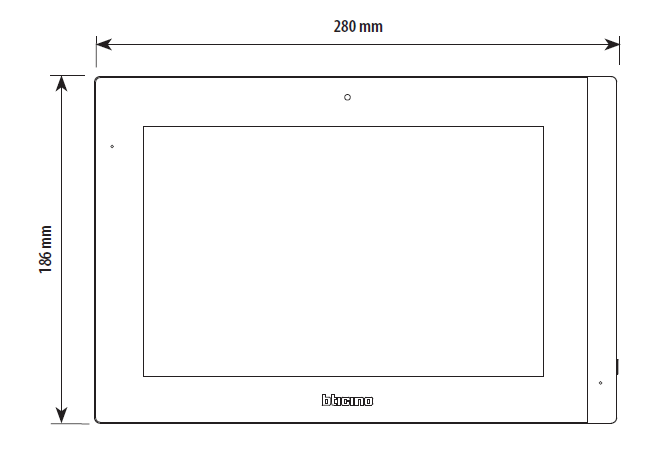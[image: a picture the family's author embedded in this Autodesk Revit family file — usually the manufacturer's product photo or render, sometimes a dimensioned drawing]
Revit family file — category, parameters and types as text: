
# Revit family: Legrand-Hotel_UX_ONE-Thermostat-With Service
name_source: partatom
category: Equipement électrique
units: mm (PartAtom-declared; Revit-internal decimal feet)

## family parameters
Configuration du panneau = Deux colonnes, circuits au sein
Cote de connecteur circulaire = Utiliser le diamètre
Couper avec des vides une fois chargée = Non
Hôte = Face
Partagée = Non
Point de calcul de pièce = Non
Type d'élément = Tableau de raccordement

## types (8) — shared parameters
Built-in depth = 50 mm  [stored 0.164042 ft]
Configurator website = https://uxforhotels.legrand.com
Do not disturb function = Oui
Elévation par défaut = 1500 mm  [stored 4.92126 ft]
Fabricant = LEGRAND
General Conditions of Use = https://export.legrand.com
Height = 93 mm  [stored 0.305118 ft]
IK = 04
IP = 20
Manual setpoint adjustment = Oui
Material = Plastic
Parallel operation possible = Oui
Radio bus system = Oui
Touchscreen = Oui
Width = 129 mm  [stored 0.423228 ft]
With display = Oui

## per-type parameters (varying)
| type | Color | Depth | Hauteur pictogrammes | Hauteur vide | Installation method | Matériau plaque | Matériau écran | Plaque apparente | Plaque encastrée | Product designation | Reference | Tension |
| Black 230V Recessed DND MUR | Black | 52 mm | 0 mm  [stored 0 ft] | -40 mm  [stored -0.131234 ft] | Flush-mounting | LEGRAND_BLACK_PLASTIC | LEGRAND_BLACK_SCREEN | Non | Oui | FLUSH MOUNTING HOTEL THERMOSTAT BLACK 230V WITH DND MUR | LG-048915 | 230 V AC |
| Black 230V Surface DND MUR | Black | 28 mm  [stored 0.0918635 ft] | 16 mm | 0 mm  [stored 0 ft] | surface | LEGRAND_BLACK_PLASTIC | LEGRAND_BLACK_SCREEN | Oui | Non | SURFACE HOTEL THERMOSTAT BLACK  230V WITH DND MUR | LG-048923 | 230 V AC |
| White 230V Recessed DND MUR | White | 52 mm | 0 mm  [stored 0 ft] | -40 mm  [stored -0.131234 ft] | Flush-mounting | LEGRAND_WHITE_PLASTIC | LEGRAND_WHITE_SCREEN | Non | Oui | FLUSH MOUNTING HOTEL THERMOSTAT WHITE 230V WITH DND MUR | LG-048924 | 230 V AC |
| White 230V Surface DND MUR | White | 28 mm  [stored 0.0918635 ft] | 16 mm | 0 mm  [stored 0 ft] | surface | LEGRAND_WHITE_PLASTIC | LEGRAND_WHITE_SCREEN | Oui | Non | SURFACE HOTEL THERMOSTAT WHITE 230V WITH DND MUR | LG-048925 | 230 V AC |
| Black 24V Recessed DND MUR | Black | 52 mm | 0 mm  [stored 0 ft] | -40 mm  [stored -0.131234 ft] | Flush-mounting | LEGRAND_BLACK_PLASTIC | LEGRAND_BLACK_SCREEN | Non | Oui | FLUSH MOUNTING HOTEL THERMOSTAT BLACK  24V WITH DND MUR | LG-048927 | 24 V |
| Black 24V Surface DND MUR | Black | 28 mm  [stored 0.0918635 ft] | 16 mm | 0 mm  [stored 0 ft] | surface | LEGRAND_BLACK_PLASTIC | LEGRAND_BLACK_SCREEN | Oui | Non | SURFACE HOTEL THERMOSTAT BLACK 24V WITH DND MUR | LG-048928 | 24 V |
| White 24V Recessed DND MUR | White | 52 mm | 0 mm  [stored 0 ft] | -40 mm  [stored -0.131234 ft] | Flush-mounting | LEGRAND_WHITE_PLASTIC | LEGRAND_WHITE_SCREEN | Non | Oui | FLUSH MOUNTING HOTEL THERMOSTAT WHITE 24V WITH DND MUR | LG-048929 | 24 V |
| White 24V Surface DND MUR | White | 28 mm  [stored 0.0918635 ft] | 16 mm | 0 mm  [stored 0 ft] | surface | LEGRAND_WHITE_PLASTIC | LEGRAND_WHITE_SCREEN | Oui | Non | SURFACE HOTEL THERMOSTAT WHITE 24V WITH DND MUR | LG-048930 | 24 V |

note: [stored X ft] marks values corroborated as IEEE doubles in the binary element streams (Revit-internal decimal feet)
